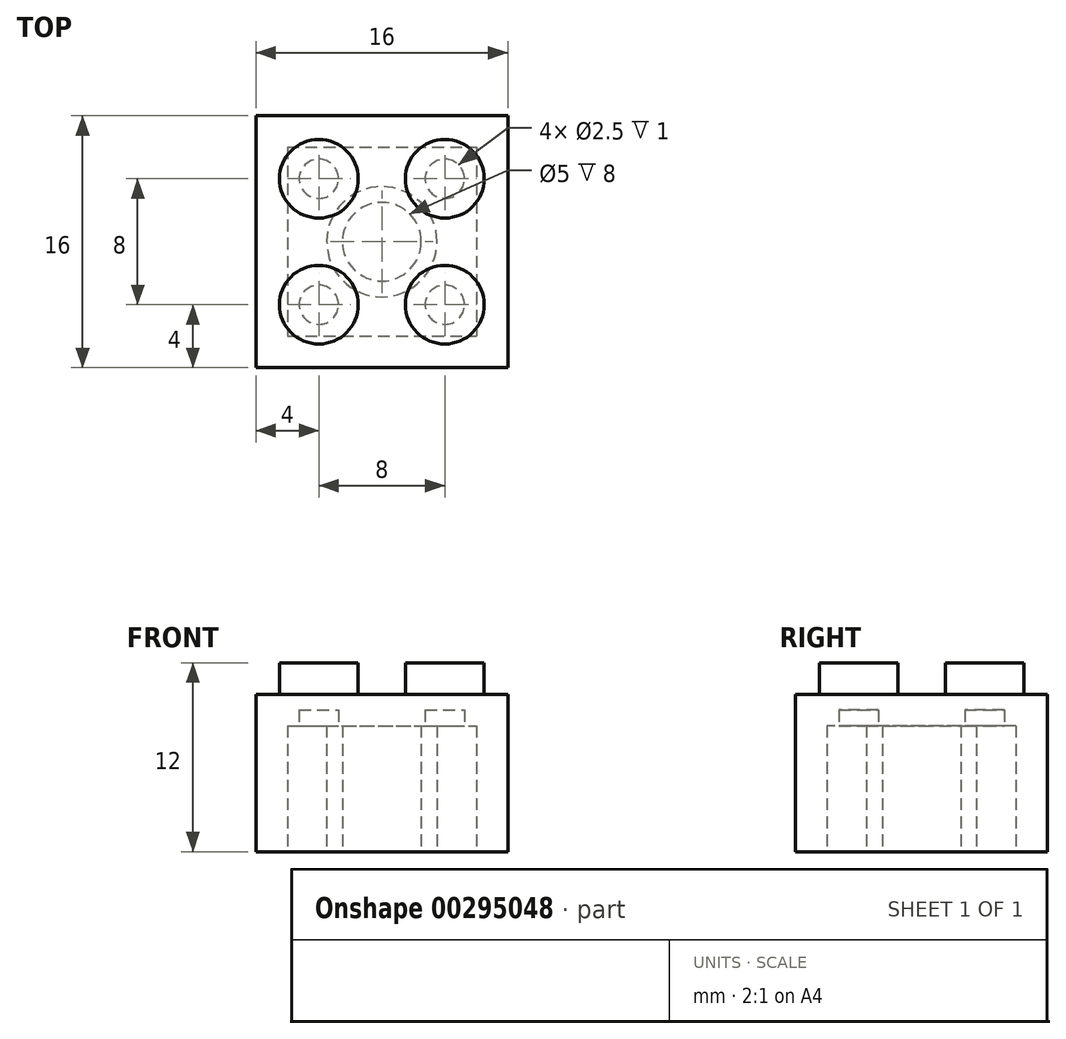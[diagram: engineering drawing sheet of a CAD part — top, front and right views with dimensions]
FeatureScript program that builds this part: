
annotation { "Feature Type Name" : "Feature", "Feature Type Description" : "" }
export const myFeature = defineFeature(function(context is Context, id is Id, definition is map)
    precondition{}
    {
        {
            var Q0;
            Q0=qCreatedBy(makeId("Front.planeOp"),FACE);
            var sketch = newSketch(context, id + "F0", { "sketchPlane" : qUnion([Q0])});
            skLineSegment(sketch, "E0.bottom", {"start": v(0, 0) * mm, "end": v(16, 0) * mm});
            skLineSegment(sketch, "E0.top", {"start": v(0, 10) * mm, "end": v(16, 10) * mm});
            skLineSegment(sketch, "E0.left", {"start": v(0, 0) * mm, "end": v(0, 10) * mm});
            skLineSegment(sketch, "E0.right", {"start": v(16, 0) * mm, "end": v(16, 10) * mm});
            skSolve(sketch);
        }
        {
            var Q0;
            Q0 = qSketchRegion(id + "F0", true);
            extrude(context, id + "F1", {"entities" : qUnion([Q0]), "depth" : 16 * mm});
        }
        {
            var Q0;
            Q0=makeQuery(id+"F1.opExtrude","SWEPT_FACE",FACE,{"disambiguationData":[OSD([sQuery(id+"F0.wireOp",EDGE,"E0.top")])]});
            var sketch = newSketch(context, id + "F2", { "sketchPlane" : qUnion([Q0])});
            skCircle(sketch, "E1", {"center": v(4, -4) * mm, "radius": 2.5 * mm});
            skCircle(sketch, "E2", {"center": v(12, -4) * mm, "radius": 2.5 * mm});
            skLineSegment(sketch, "E3", {"start": v(0, -8) * mm, "end": v(16, -8) * mm});
            skCircle(sketch, "E4.MirrorC", {"center": v(4, -12) * mm, "radius": 2.5 * mm});
            skCircle(sketch, "E5.MirrorC", {"center": v(12, -12) * mm, "radius": 2.5 * mm});
            skSolve(sketch);
        }
        {
            var Q0;
            Q0 = qSketchRegion(id + "F2", true);
            extrude(context, id + "F3", {"entities" : qUnion([Q0]), "operationType" : NewBodyOperationType.ADD, "depth" : 2 * mm});
        }
        {
            var Q0;
            Q0=makeQuery(id+"F1.opExtrude","SWEPT_FACE",FACE,{"disambiguationData":[OSD([sQuery(id+"F0.wireOp",EDGE,"E0.bottom")])]});
            var sketch = newSketch(context, id + "F4", { "sketchPlane" : qUnion([Q0])});
            skLineSegment(sketch, "E6.bottom", {"start": v(2, 2) * mm, "end": v(14, 2) * mm});
            skLineSegment(sketch, "E6.top", {"start": v(2, 14) * mm, "end": v(14, 14) * mm});
            skLineSegment(sketch, "E6.left", {"start": v(2, 2) * mm, "end": v(2, 14) * mm});
            skLineSegment(sketch, "E6.right", {"start": v(14, 2) * mm, "end": v(14, 14) * mm});
            skSolve(sketch);
        }
        {
            var Q0;
            Q0=makeQuery(id+"F4.imprint","IMPRINT",FACE,{"disambiguationData":[TD([[makeQuery(id+"F4.imprint","IMPRINT",EDGE,{"derivedFrom":sQuery(id+"F4.wireOp",EDGE,"E6.bottom")}),1.0]])]});
            var sketch = newSketch(context, id + "F5", { "sketchPlane" : qUnion([Q0])});
            skCircle(sketch, "E7", {"center": v(8, 8) * mm, "radius": 3.5 * mm});
            skCircle(sketch, "E8", {"center": v(8, 8) * mm, "radius": 2.5 * mm});
            skSolve(sketch);
        }
        {
            var Q0;
            Q0=makeQuery(id+"F5.imprint","IMPRINT",FACE,{"disambiguationData":[TD([[makeQuery(id+"F5.imprint","IMPRINT",EDGE,{"derivedFrom":sQuery(id+"F5.wireOp",EDGE,"E7")}),-1.0]])]});
            var Q1;
            Q1=makeQuery(id+"F5.imprint","IMPRINT",FACE,{"disambiguationData":[TD([[makeQuery(id+"F5.imprint","IMPRINT",EDGE,{"derivedFrom":sQuery(id+"F5.wireOp",EDGE,"E8")}),1.0]])]});
            extrude(context, id + "F6", {"entities" : qUnion([Q0, Q1]), "operationType" : NewBodyOperationType.REMOVE, "oppositeDirection" : true, "depth" : 8 * mm});
        }
        {
            var Q0;
            Q0=makeQuery(id+"F5.imprint","IMPRINT",FACE,{"disambiguationData":[TD([[makeQuery(id+"F5.imprint","IMPRINT",EDGE,{"derivedFrom":sQuery(id+"F5.wireOp",EDGE,"E7")}),-1.0]])]});
            var sketch = newSketch(context, id + "F7", { "sketchPlane" : qUnion([Q0])});
            skCircle(sketch, "E9", {"center": v(12, 12) * mm, "radius": 1.25 * mm});
            skCircle(sketch, "E10", {"center": v(4, 12) * mm, "radius": 1.25 * mm});
            skCircle(sketch, "E11", {"center": v(4, 4) * mm, "radius": 1.25 * mm});
            skCircle(sketch, "E12", {"center": v(12, 4) * mm, "radius": 1.25 * mm});
            skSolve(sketch);
        }
        {
            var Q0;
            Q0 = qSketchRegion(id + "F7", true);
            extrude(context, id + "F8", {"entities" : qUnion([Q0]), "operationType" : NewBodyOperationType.REMOVE, "oppositeDirection" : true, "depth" : 9 * mm});
        }
    });
